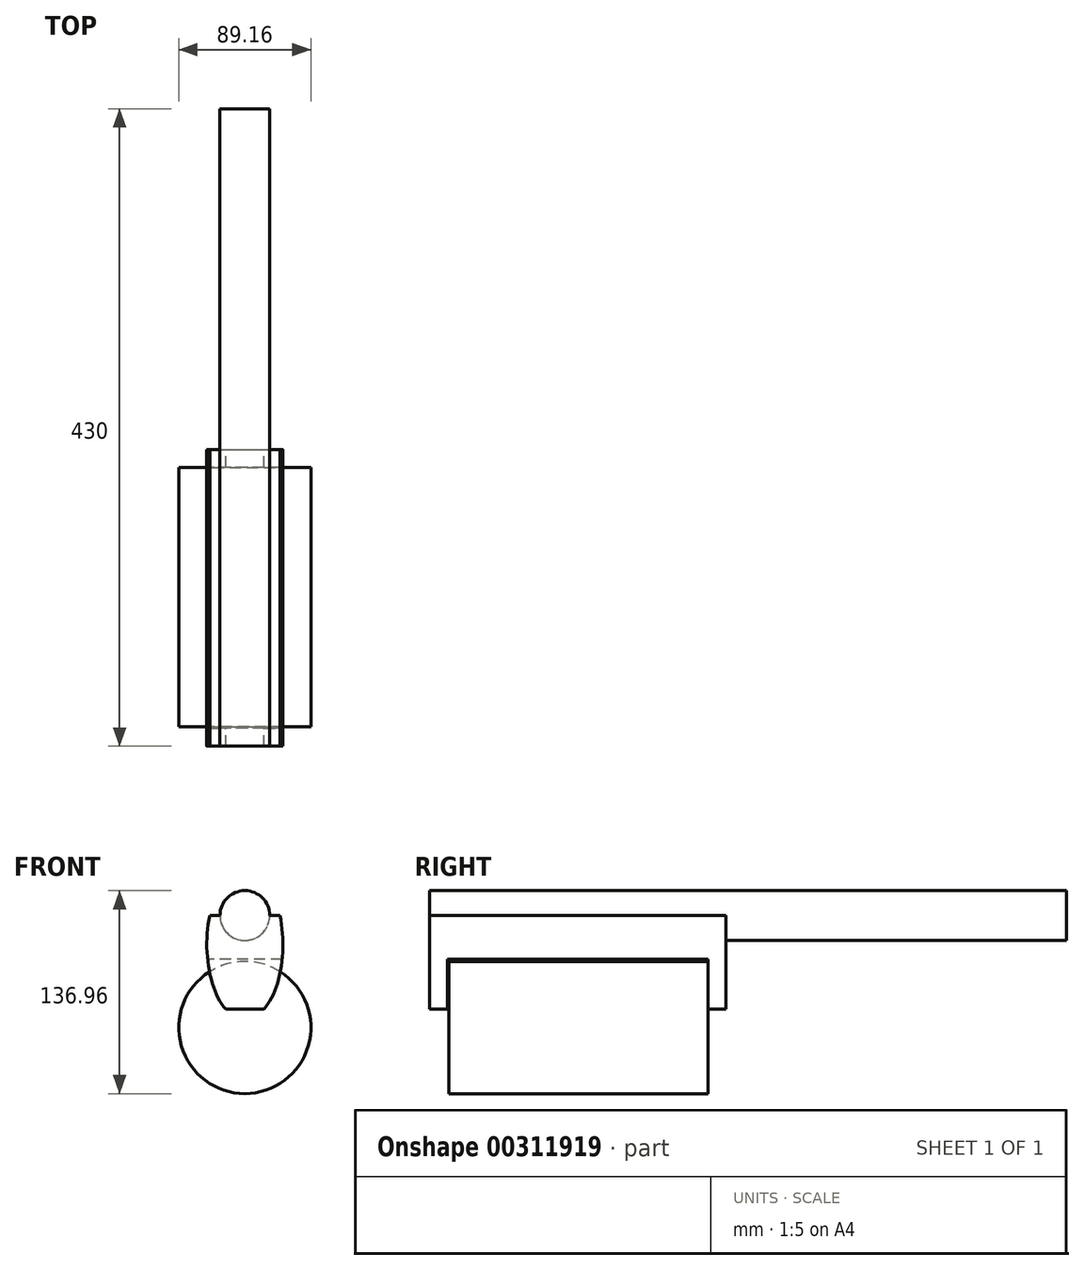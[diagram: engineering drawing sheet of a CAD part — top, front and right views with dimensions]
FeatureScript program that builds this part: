
annotation { "Feature Type Name" : "Feature", "Feature Type Description" : "" }
export const myFeature = defineFeature(function(context is Context, id is Id, definition is map)
    precondition{}
    {
        {
            var Q0;
            Q0=qCreatedBy(makeId("Front.planeOp"),FACE);
            var sketch = newSketch(context, id + "F0", { "sketchPlane" : qUnion([Q0])});
            skLineSegment(sketch, "E0.top", {"start": v(-12.94, -43.72) * mm, "end": v(12.94, -43.72) * mm});
            skPoint(sketch, "E0.middle", {"position": v(0, 0) * mm});
            skEllipticalArc(sketch, "E1", {});
            skLineSegment(sketch, "E2", {"start": v(-23.68, 19.55) * mm, "end": v(23.68, 19.55) * mm});
            skLineSegment(sketch, "E3", {"start": v(23.68, 19.55) * mm, "end": v(-23.68, 19.55) * mm});
            skPoint(sketch, "E0.left.start.orphan", {"position": v(-25.82, 43.72) * mm});
            skPoint(sketch, "E0.right.start.orphan", {"position": v(25.82, 43.72) * mm});
            skPoint(sketch, "E4.orphan", {"position": v(25.82, -43.72) * mm});
            skPoint(sketch, "E5.orphan", {"position": v(-25.82, -43.72) * mm});
            skEllipticalArc(sketch, "E6.trimOffspring", {});
            const initialGuessF0  = {"E1": [0, 0, 0, 1, 0.05062500014901161, 0.02566900165163322, 1.1743261984695261, 2.613235356124422], "E6.trimOffspring": [0, 0, 0, 1, 0.05062500014901161, 0.02566900165163322, 3.669949951055163, 5.108859108710061]};
            skSetInitialGuess(sketch, initialGuessF0);
            skSolve(sketch);
        }
        {
            var Q0;
            Q0=makeQuery(id+"F0.imprint","IMPRINT",FACE,{"disambiguationData":[TD([[makeQuery(id+"F0.imprint","IMPRINT",EDGE,{"derivedFrom":sQuery(id+"F0.wireOp",EDGE,"E0.top")}),1.0]])]});
            extrude(context, id + "F1", {"entities" : qUnion([Q0]), "depth" : 200 * mm});
        }
        {
            var Q0;
            Q0=qCreatedBy(makeId("Front.planeOp"),FACE);
            cPlane(context, id + "F2", {"entities" : qUnion([Q0]), "cplaneType" : CPlaneType.OFFSET, "offset" : 230 * mm, "oppositeDirection" : true, "width" : 150 * mm, "height" : 150 * mm});
        }
        {
            var Q0;
            Q0=qCreatedBy(id+"F2.planeOp",FACE);
            var sketch = newSketch(context, id + "F3", { "sketchPlane" : qUnion([Q0])});
            skCircle(sketch, "E7", {"center": v(0, 19.53) * mm, "radius": 16.8 * mm});
            skSolve(sketch);
        }
        {
            var Q0;
            Q0=makeQuery(id+"F3.imprint","IMPRINT",FACE,{"disambiguationData":[TD([[makeQuery(id+"F3.imprint","IMPRINT",EDGE,{"derivedFrom":sQuery(id+"F3.wireOp",EDGE,"E7")}),1.0]])]});
            extrude(context, id + "F4", {"entities" : qUnion([Q0]), "operationType" : NewBodyOperationType.ADD, "depth" : 430 * mm});
        }
        {
            var Q0;
            Q0=qCreatedBy(makeId("Right.planeOp"),FACE);
            cPlane(context, id + "F5", {"entities" : qUnion([Q0]), "cplaneType" : CPlaneType.OFFSET, "offset" : 30 * mm, "oppositeDirection" : true, "width" : 150 * mm, "height" : 150 * mm});
        }
        {
            var Q0;
            Q0=qCreatedBy(id+"F5.planeOp",FACE);
            var sketch = newSketch(context, id + "F6", { "sketchPlane" : qUnion([Q0])});
            skLineSegment(sketch, "E8.bottom", {"start": v(-11.94, -9.83) * mm, "end": v(-187.94, -9.83) * mm});
            skLineSegment(sketch, "E8.top", {"start": v(-11.94, -77.67) * mm, "end": v(-187.94, -77.67) * mm});
            skLineSegment(sketch, "E8.left", {"start": v(-11.94, -9.83) * mm, "end": v(-11.94, -77.67) * mm});
            skLineSegment(sketch, "E8.right", {"start": v(-187.94, -9.83) * mm, "end": v(-187.94, -77.67) * mm});
            skPoint(sketch, "E8.middle", {"position": v(-99.94, -43.75) * mm});
            skPoint(sketch, "E9.orphan", {"position": v(0, -43.75) * mm});
            skPoint(sketch, "E10.orphan", {"position": v(-199.89, -43.75) * mm});
            skSolve(sketch);
        }
        {
            var Q0;
            Q0=makeQuery(id+"F6.imprint","IMPRINT",FACE,{"disambiguationData":[TD([[makeQuery(id+"F6.imprint","IMPRINT",EDGE,{"derivedFrom":sQuery(id+"F6.wireOp",EDGE,"E8.bottom")}),1.0]])]});
            extrude(context, id + "F7", {"entities" : qUnion([Q0]), "operationType" : NewBodyOperationType.REMOVE, "depth" : 100 * mm});
        }
        {
            var Q0;
            Q0=makeQuery(id+"F7.boolean.opBoolean","COPY",FACE,{"derivedFrom":makeQuery(id+"F7.opExtrude","SWEPT_FACE",FACE,{"disambiguationData":[OSD([sQuery(id+"F6.wireOp",EDGE,"E8.left")])]})});
            var sketch = newSketch(context, id + "F8", { "sketchPlane" : qUnion([Q0])});
            skPoint(sketch, "E11.endSnap0", {"position": v(0, -43.72) * mm});
            skCircle(sketch, "E12", {"center": v(0, -56.06) * mm, "radius": 44.58 * mm});
            skPoint(sketch, "E11.start.orphan", {"position": v(0, -43.72) * mm});
            skSolve(sketch);
        }
        {
            var Q0;
            {var subQ1=makeQuery(id+"F7.opExtrude","SWEPT_FACE",FACE,{"disambiguationData":[OSD([sQuery(id+"F6.wireOp",EDGE,"E8.left")])]});var subQ6=makeQuery(id+"F7.boolean.opBoolean","INTERSECT",EDGE,{"derivedFrom":[makeQuery(id+"F1.opExtrude","SWEPT_FACE",FACE,{"disambiguationData":[OSD([sQuery(id+"F0.wireOp",EDGE,"E0.top")])]}),subQ1]});Q0=makeQuery(id+"F8.imprint","IMPRINT",FACE,{"disambiguationData":[TD([[makeQuery(id+"F8.imprint","IMPRINT",EDGE,{"derivedFrom":subQ6}),-1.0]])]});}
            var Q1;
            {var subQ1=makeQuery(id+"F7.opExtrude","SWEPT_FACE",FACE,{"disambiguationData":[OSD([sQuery(id+"F6.wireOp",EDGE,"E8.left")])]});var subQ6=makeQuery(id+"F7.boolean.opBoolean","INTERSECT",EDGE,{"derivedFrom":[makeQuery(id+"F1.opExtrude","SWEPT_FACE",FACE,{"disambiguationData":[OSD([sQuery(id+"F0.wireOp",EDGE,"E0.top")])]}),subQ1]});Q1=makeQuery(id+"F8.imprint","IMPRINT",FACE,{"disambiguationData":[TD([[makeQuery(id+"F8.imprint","IMPRINT",EDGE,{"derivedFrom":subQ6}),1.0]])]});}
            extrude(context, id + "F9", {"entities" : qUnion([Q0, Q1]), "operationType" : NewBodyOperationType.ADD, "depth" : 175 * mm});
        }
    });
